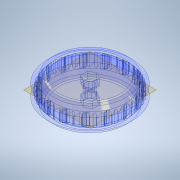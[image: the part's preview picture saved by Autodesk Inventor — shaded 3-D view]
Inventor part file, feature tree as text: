
AUTODESK INVENTOR PART (.ipt)
format: ipt  version: 2022 (Build 260153000, 153)  size: 644,608 bytes
history: native  units: in
note: dims shown in document units (in); Inventor stores cm internally (conversion verified against a paired STEP export)
features: extrude x5, sketch x4, fillet x2, pattern_circular x2, projected_geometry x2, revolve x1, chamfer x1, plane x1
ambient origin geometry x8: Origin, YZ Plane, XZ Plane, XY Plane, X Axis, Y Axis, Z Axis, Center Point
bodies: Solid1 (feature_tree)
feature tree (18):
  revolve  "Revolution1"  [1 undecoded]
  extrude  "Extrusion1"  Depth=0.75in
  fillet  "Fillet2"  Radius=0.25in
  pattern_circular  "Circular Pattern1"  Angle=90.0deg  [1 undecoded]
  extrude  "Extrusion2"  Depth=0.2in
  fillet  "Fillet1"  [1 undecoded]
  pattern_circular  "Circular Pattern2"  [2 undecoded]
  chamfer  "Chamfer1"  Distance=17.7165in Angle=360.0deg
  plane  "Work Plane1"
  sketch  "Sketch5"  dims[d6=0.04in d7=90.0deg d8=0.075in d9=60.0deg d10=0.75in d11=0.0in d12=17.7165in d13=360.0deg d15=0.02in d16=0.0344in d17=0.015in d19=0.25in d20=0.0in d21=0.0025in d22=0.025in d23=0.02in d24=5.9055in d25=360.0deg d27=0.125in d28=0.125in d29=45.0deg d38=-0.25in d39=0.25in d40=0.02in d41=0.02in d46=0.0in d47=0.0in d54=0.2in d55=0.0in d56=0.0in d57=0.0in]
  extrude  "Extrusion6"  Depth=0.2in
  extrude  "Extrusion10"  Depth=0.2in
  extrude  "Extrusion11"  Depth=0.2in
  sketch  "Sketch1"  dims[d0=0.5in d1=0.9in]
  sketch  "Sketch2"  dims[d2=0.3436in d3=0.75in d4=0.25in]
  sketch  "Sketch3"  dims[d5=0.1in]
  projected_geometry  "Projected Loop1"
  projected_geometry  "Projected Loop2"
note: 5 required parameter values undecoded (feature->parameter linkage not recoverable at this tier; creation-order binding heuristic only, values carry confidence <= 0.55)